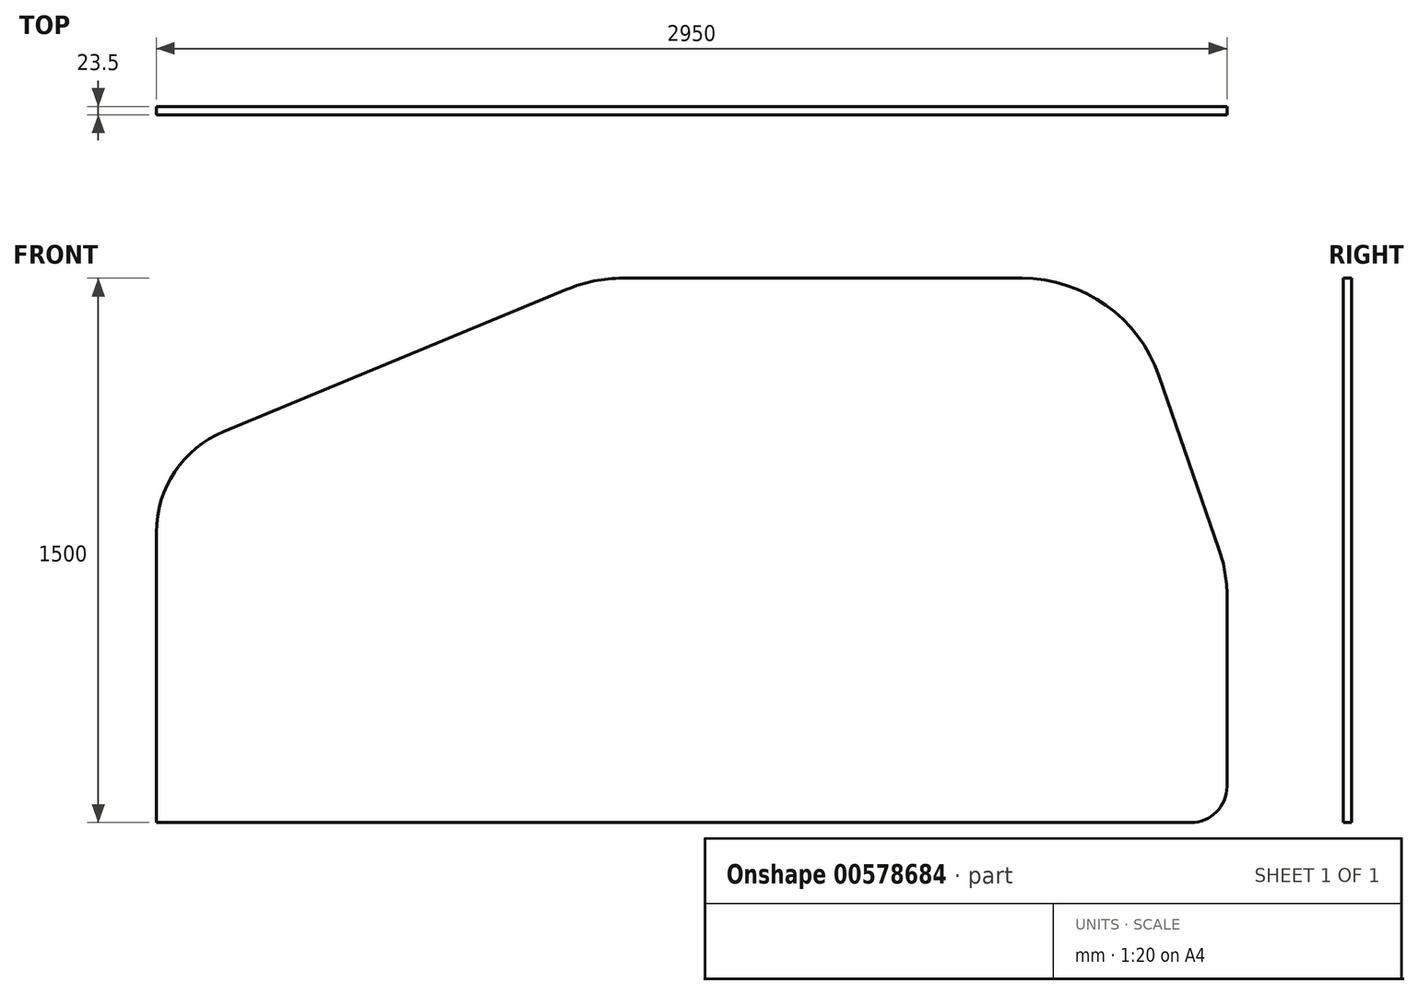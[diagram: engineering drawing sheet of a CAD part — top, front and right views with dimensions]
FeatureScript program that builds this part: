
annotation { "Feature Type Name" : "Feature", "Feature Type Description" : "" }
export const myFeature = defineFeature(function(context is Context, id is Id, definition is map)
    precondition{}
    {
        {
            var Q0;
            Q0=qCreatedBy(makeId("Front.planeOp"),FACE);
            var sketch = newSketch(context, id + "F0", { "sketchPlane" : qUnion([Q0])});
            skLineSegment(sketch, "E0", {"start": v(0, 0) * mm, "end": v(2850, 0) * mm});
            skLineSegment(sketch, "E1", {"start": v(0, 0) * mm, "end": v(0, 0) * mm});
            skLineSegment(sketch, "E2", {"start": v(1284.46, 1500) * mm, "end": v(2384.46, 1500) * mm});
            skLineSegment(sketch, "E3", {"start": v(2762.35, 1231.12) * mm, "end": v(2927.9, 754.03) * mm});
            skLineSegment(sketch, "E4", {"start": v(2950, 622.9) * mm, "end": v(2950, 100) * mm});
            skArc(sketch, "E5.filletArc", {"start": v(1284.46, 1500) * mm, "mid": v(1206.34, 1492.3) * mm, "end": v(1131.23, 1469.49) * mm});
            skPoint(sketch, "E6.visualSharp", {"position": v(2626.03, 1624) * mm});
            skArc(sketch, "E6.filletArc", {"start": v(2762.35, 1231.12) * mm, "mid": v(2616.35, 1425.92) * mm, "end": v(2384.46, 1500) * mm});
            skArc(sketch, "E7.filletArc", {"start": v(2950, 622.9) * mm, "mid": v(2944.44, 689.4) * mm, "end": v(2927.9, 754.03) * mm});
            skPoint(sketch, "E8.visualSharp", {"position": v(0, 0) * mm});
            skArc(sketch, "E9.filletArc", {"start": v(2850, 0) * mm, "mid": v(2920.71, 29.29) * mm, "end": v(2950, 100) * mm});
            skLineSegment(sketch, "E10", {"start": v(0, 0) * mm, "end": v(0, 800) * mm});
            skLineSegment(sketch, "E11", {"start": v(1131.23, 1469.49) * mm, "end": v(185.08, 1077.12) * mm});
            skArc(sketch, "E12", {"start": v(185.08, 1077.12) * mm, "mid": v(50.52, 966.62) * mm, "end": v(0, 800) * mm});
            skSolve(sketch);
        }
        {
            var Q0;
            Q0 = qSketchRegion(id + "F0", true);
            extrude(context, id + "F1", {"entities" : qUnion([Q0]), "depth" : 23.5 * mm, "offsetDistance" : 25 * mm});
        }
    });
